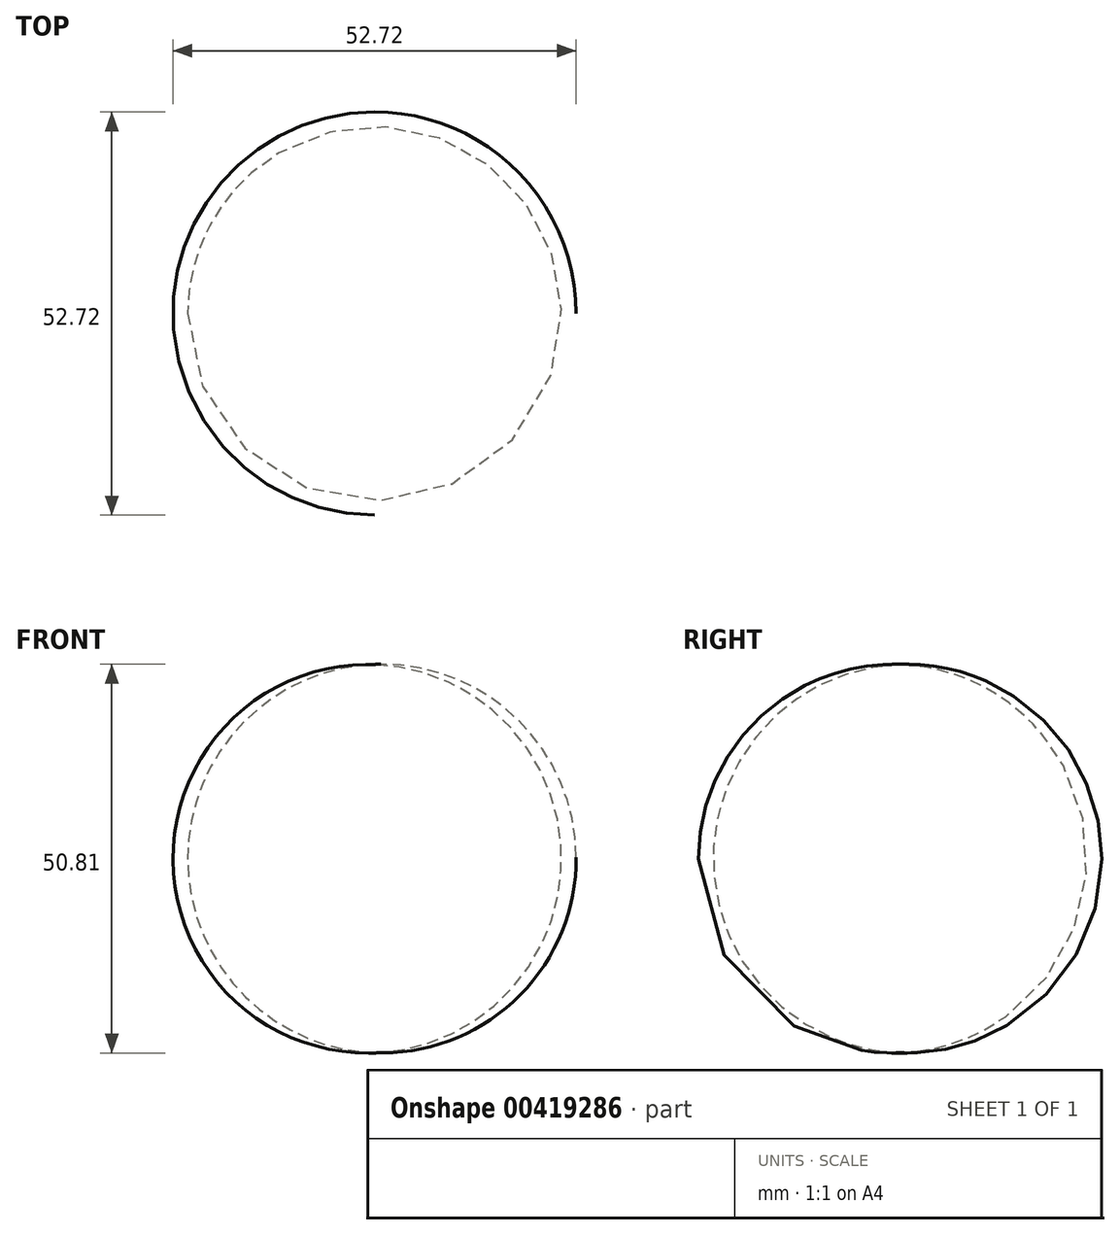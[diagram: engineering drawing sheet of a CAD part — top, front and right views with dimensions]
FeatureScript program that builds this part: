
annotation { "Feature Type Name" : "Feature", "Feature Type Description" : "" }
export const myFeature = defineFeature(function(context is Context, id is Id, definition is map)
    precondition{}
    {
        {
            var Q0;
            Q0=qCreatedBy(makeId("Front.planeOp"),FACE);
            var sketch = newSketch(context, id + "F0", { "sketchPlane" : qUnion([Q0])});
            skArc(sketch, "E0", {"start": v(0.8, 25.39) * mm, "mid": v(-25.4, -0.17) * mm, "end": v(1.13, -25.37) * mm});
            skLineSegment(sketch, "E1", {"start": v(0.8, 25.39) * mm, "end": v(1.13, -25.37) * mm});
            skSolve(sketch);
        }
        {
            var Q0;
            Q0=makeQuery(id+"F0.imprint","IMPRINT",FACE,{"disambiguationData":[TD([[makeQuery(id+"F0.imprint","IMPRINT",EDGE,{"derivedFrom":sQuery(id+"F0.wireOp",EDGE,"E0")}),1.0]])]});
            var Q1;
            Q1=sQuery(id+"F0.wireOp",EDGE,"E1");
            revolve(context, id + "F1", {"entities" : qUnion([Q0]), "axis" : qUnion([Q1]), "revolveType" : RevolveType.FULL});
        }
    });
